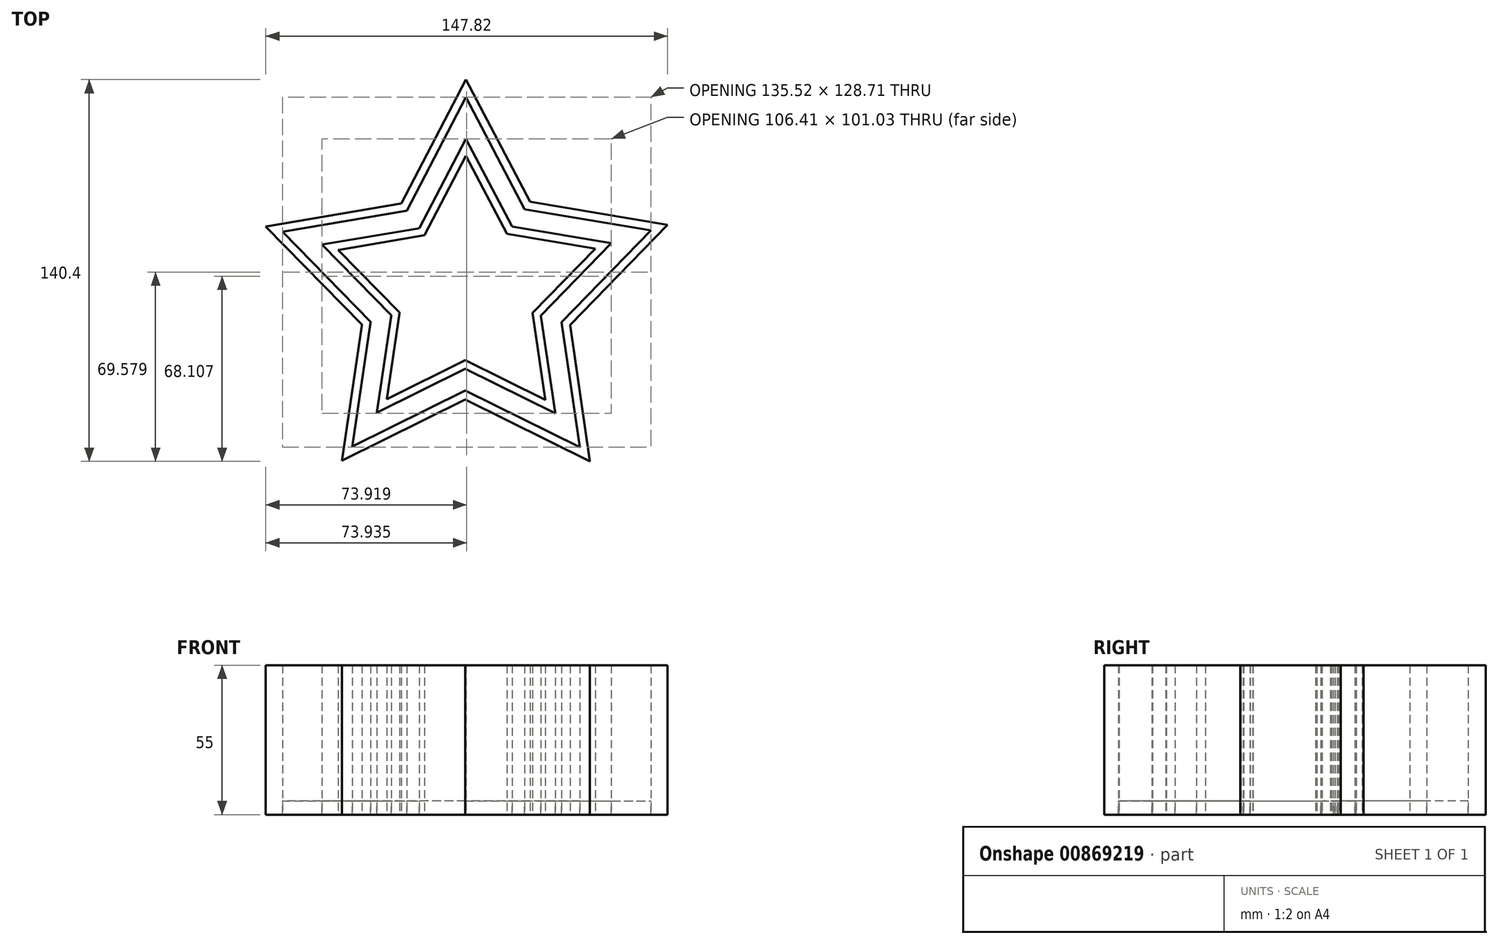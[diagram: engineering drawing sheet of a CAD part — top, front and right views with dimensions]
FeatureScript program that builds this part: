
annotation { "Feature Type Name" : "Feature", "Feature Type Description" : "" }
export const myFeature = defineFeature(function(context is Context, id is Id, definition is map)
    precondition{}
    {
        {
            var Q0;
            Q0=qCreatedBy(makeId("Top.planeOp"),FACE);
            var sketch = newSketch(context, id + "F0", { "sketchPlane" : qUnion([Q0])});
            skLineSegment(sketch, "E0", {"start": v(-71.32, 23.12) * mm, "end": v(-22.82, 31.37) * mm});
            skLineSegment(sketch, "E1", {"start": v(0.3, 75.62) * mm, "end": v(-22.82, 31.37) * mm});
            skLineSegment(sketch, "E2", {"start": v(0.3, 75.62) * mm, "end": v(23.21, 31.91) * mm});
            skLineSegment(sketch, "E3", {"start": v(23.21, 31.91) * mm, "end": v(72.4, 23.7) * mm});
            skLineSegment(sketch, "E4", {"start": v(37.54, -12.17) * mm, "end": v(72.4, 23.7) * mm});
            skLineSegment(sketch, "E5", {"start": v(37.54, -12.17) * mm, "end": v(44.64, -60.9) * mm});
            skLineSegment(sketch, "E6", {"start": v(44.64, -60.9) * mm, "end": v(0, -38.8) * mm});
            skLineSegment(sketch, "E7", {"start": v(0, -38.8) * mm, "end": v(-44.03, -60.68) * mm});
            skLineSegment(sketch, "E8", {"start": v(-44.03, -60.68) * mm, "end": v(-36.89, -12) * mm});
            skLineSegment(sketch, "E9", {"start": v(-36.89, -12) * mm, "end": v(-71.32, 23.12) * mm});
            skLineSegment(sketch, "E10.0", {"start": v(-41.5, -57.19) * mm, "end": v(-34.76, -11.32) * mm});
            skLineSegment(sketch, "E10.1", {"start": v(0, -36.56) * mm, "end": v(-41.5, -57.19) * mm});
            skLineSegment(sketch, "E10.2", {"start": v(-34.76, -11.32) * mm, "end": v(-67.21, 21.8) * mm});
            skLineSegment(sketch, "E10.3", {"start": v(42.1, -57.4) * mm, "end": v(0, -36.56) * mm});
            skLineSegment(sketch, "E10.4", {"start": v(35.42, -11.48) * mm, "end": v(42.1, -57.4) * mm});
            skLineSegment(sketch, "E10.5", {"start": v(35.42, -11.48) * mm, "end": v(68.3, 22.35) * mm});
            skLineSegment(sketch, "E10.6", {"start": v(-67.21, 21.8) * mm, "end": v(-21.5, 29.56) * mm});
            skLineSegment(sketch, "E10.7", {"start": v(0.3, 71.3) * mm, "end": v(-21.5, 29.56) * mm});
            skLineSegment(sketch, "E10.8", {"start": v(0.3, 71.3) * mm, "end": v(21.9, 30.1) * mm});
            skLineSegment(sketch, "E10.9", {"start": v(21.9, 30.1) * mm, "end": v(68.3, 22.35) * mm});
            skLineSegment(sketch, "E11.0", {"start": v(0.3, 56) * mm, "end": v(17.25, 23.68) * mm});
            skLineSegment(sketch, "E11.1", {"start": v(17.25, 23.68) * mm, "end": v(53.77, 17.58) * mm});
            skLineSegment(sketch, "E11.2", {"start": v(0.3, 56) * mm, "end": v(-16.84, 23.16) * mm});
            skLineSegment(sketch, "E11.3", {"start": v(27.89, -9.04) * mm, "end": v(53.77, 17.58) * mm});
            skLineSegment(sketch, "E11.4", {"start": v(27.89, -9.04) * mm, "end": v(33.13, -45.04) * mm});
            skLineSegment(sketch, "E11.5", {"start": v(33.13, -45.04) * mm, "end": v(0, -28.63) * mm});
            skLineSegment(sketch, "E11.6", {"start": v(-52.64, 17.07) * mm, "end": v(-16.84, 23.16) * mm});
            skLineSegment(sketch, "E11.7", {"start": v(-27.23, -8.86) * mm, "end": v(-52.64, 17.07) * mm});
            skLineSegment(sketch, "E11.8", {"start": v(-32.5, -44.79) * mm, "end": v(-27.23, -8.86) * mm});
            skLineSegment(sketch, "E11.9", {"start": v(0, -28.63) * mm, "end": v(-32.5, -44.79) * mm});
            skLineSegment(sketch, "E12.0", {"start": v(0.31, 50.82) * mm, "end": v(15.68, 21.51) * mm});
            skLineSegment(sketch, "E12.1", {"start": v(15.68, 21.51) * mm, "end": v(48.86, 15.97) * mm});
            skLineSegment(sketch, "E12.2", {"start": v(0.31, 50.82) * mm, "end": v(-15.27, 20.99) * mm});
            skLineSegment(sketch, "E12.3", {"start": v(25.34, -8.22) * mm, "end": v(48.86, 15.97) * mm});
            skLineSegment(sketch, "E12.4", {"start": v(25.34, -8.22) * mm, "end": v(30.1, -40.86) * mm});
            skLineSegment(sketch, "E12.5", {"start": v(30.1, -40.86) * mm, "end": v(-0.01, -25.95) * mm});
            skLineSegment(sketch, "E12.6", {"start": v(-47.72, 15.47) * mm, "end": v(-15.27, 20.99) * mm});
            skLineSegment(sketch, "E12.7", {"start": v(-24.68, -8.04) * mm, "end": v(-47.72, 15.47) * mm});
            skLineSegment(sketch, "E12.8", {"start": v(-29.46, -40.6) * mm, "end": v(-24.68, -8.04) * mm});
            skLineSegment(sketch, "E12.9", {"start": v(-0.01, -25.95) * mm, "end": v(-29.46, -40.6) * mm});
            skSolve(sketch);
        }
        {
            var Q0;
            Q0=makeQuery(id+"F0.imprint","IMPRINT",FACE,{"disambiguationData":[TD([[makeQuery(id+"F0.imprint","IMPRINT",EDGE,{"derivedFrom":sQuery(id+"F0.wireOp",EDGE,"E10.0")}),-1.0]])]});
            extrude(context, id + "F1", {"entities" : qUnion([Q0]), "oppositeDirection" : true, "depth" : 5 * mm, "offsetDistance" : 25 * mm});
        }
        {
            var Q0;
            Q0=makeQuery(id+"F1.opExtrude","CAP_FACE",FACE,{"disambiguationData":[OSD([sQuery(id+"F0.wireOp",EDGE,"E10.0"),sQuery(id+"F0.wireOp",EDGE,"E10.1"),sQuery(id+"F0.wireOp",EDGE,"E10.2"),sQuery(id+"F0.wireOp",EDGE,"E10.3"),sQuery(id+"F0.wireOp",EDGE,"E10.4"),sQuery(id+"F0.wireOp",EDGE,"E10.5"),sQuery(id+"F0.wireOp",EDGE,"E10.6"),sQuery(id+"F0.wireOp",EDGE,"E10.7"),sQuery(id+"F0.wireOp",EDGE,"E10.8"),sQuery(id+"F0.wireOp",EDGE,"E10.9"),sQuery(id+"F0.wireOp",EDGE,"E11.0"),sQuery(id+"F0.wireOp",EDGE,"E11.1"),sQuery(id+"F0.wireOp",EDGE,"E11.2"),sQuery(id+"F0.wireOp",EDGE,"E11.3"),sQuery(id+"F0.wireOp",EDGE,"E11.4"),sQuery(id+"F0.wireOp",EDGE,"E11.5"),sQuery(id+"F0.wireOp",EDGE,"E11.6"),sQuery(id+"F0.wireOp",EDGE,"E11.7"),sQuery(id+"F0.wireOp",EDGE,"E11.8"),sQuery(id+"F0.wireOp",EDGE,"E11.9")])],"isStart":false});
            var sketch = newSketch(context, id + "F2", { "sketchPlane" : qUnion([Q0])});
            skLineSegment(sketch, "E13.0", {"start": v(47.83, -15.63) * mm, "end": v(24.8, 8.05) * mm});
            skLineSegment(sketch, "E13.1", {"start": v(24.8, 8.05) * mm, "end": v(29.46, 39.99) * mm});
            skLineSegment(sketch, "E13.2", {"start": v(15.35, -21.06) * mm, "end": v(47.83, -15.63) * mm});
            skLineSegment(sketch, "E13.3", {"start": v(29.46, 39.99) * mm, "end": v(-0.01, 25.4) * mm});
            skLineSegment(sketch, "E13.4", {"start": v(-0.01, 25.4) * mm, "end": v(-28.83, 39.72) * mm});
            skLineSegment(sketch, "E13.5", {"start": v(-28.83, 39.72) * mm, "end": v(-24.15, 7.86) * mm});
            skLineSegment(sketch, "E13.6", {"start": v(0.31, -49.74) * mm, "end": v(15.35, -21.06) * mm});
            skLineSegment(sketch, "E13.7", {"start": v(-14.94, -20.54) * mm, "end": v(0.31, -49.74) * mm});
            skLineSegment(sketch, "E13.8", {"start": v(-46.69, -15.14) * mm, "end": v(-14.94, -20.54) * mm});
            skLineSegment(sketch, "E13.9", {"start": v(-24.15, 7.86) * mm, "end": v(-46.69, -15.14) * mm});
            skLineSegment(sketch, "E14.0", {"start": v(74.45, -24.37) * mm, "end": v(38.6, 12.52) * mm});
            skLineSegment(sketch, "E14.1", {"start": v(38.6, 12.52) * mm, "end": v(45.9, 62.63) * mm});
            skLineSegment(sketch, "E14.2", {"start": v(23.87, -32.82) * mm, "end": v(74.45, -24.37) * mm});
            skLineSegment(sketch, "E14.3", {"start": v(45.9, 62.63) * mm, "end": v(0, 39.9) * mm});
            skLineSegment(sketch, "E14.4", {"start": v(0, 39.9) * mm, "end": v(-45.3, 62.43) * mm});
            skLineSegment(sketch, "E14.5", {"start": v(-45.3, 62.43) * mm, "end": v(-37.95, 12.35) * mm});
            skLineSegment(sketch, "E14.6", {"start": v(0.3, -77.77) * mm, "end": v(23.87, -32.82) * mm});
            skLineSegment(sketch, "E14.7", {"start": v(-23.48, -32.27) * mm, "end": v(0.3, -77.77) * mm});
            skLineSegment(sketch, "E14.8", {"start": v(-73.37, -23.8) * mm, "end": v(-23.48, -32.27) * mm});
            skLineSegment(sketch, "E14.9", {"start": v(-37.95, 12.35) * mm, "end": v(-73.37, -23.8) * mm});
            skSolve(sketch);
        }
        {
            var Q0;
            Q0=makeQuery(id+"F2.imprint","IMPRINT",FACE,{"disambiguationData":[TD([[makeQuery(id+"F2.imprint","IMPRINT",EDGE,{"derivedFrom":sQuery(id+"F2.wireOp",EDGE,"E14.0")}),1.0]])]});
            var Q1;
            Q1=makeQuery(id+"F2.imprint","IMPRINT",FACE,{"disambiguationData":[TD([[makeQuery(id+"F2.imprint","IMPRINT",EDGE,{"derivedFrom":sQuery(id+"F2.wireOp",EDGE,"E13.0")}),-1.0]])]});
            extrude(context, id + "F3", {"entities" : qUnion([Q0, Q1]), "oppositeDirection" : true, "depth" : 55 * mm, "offsetDistance" : 25 * mm});
        }
    });
